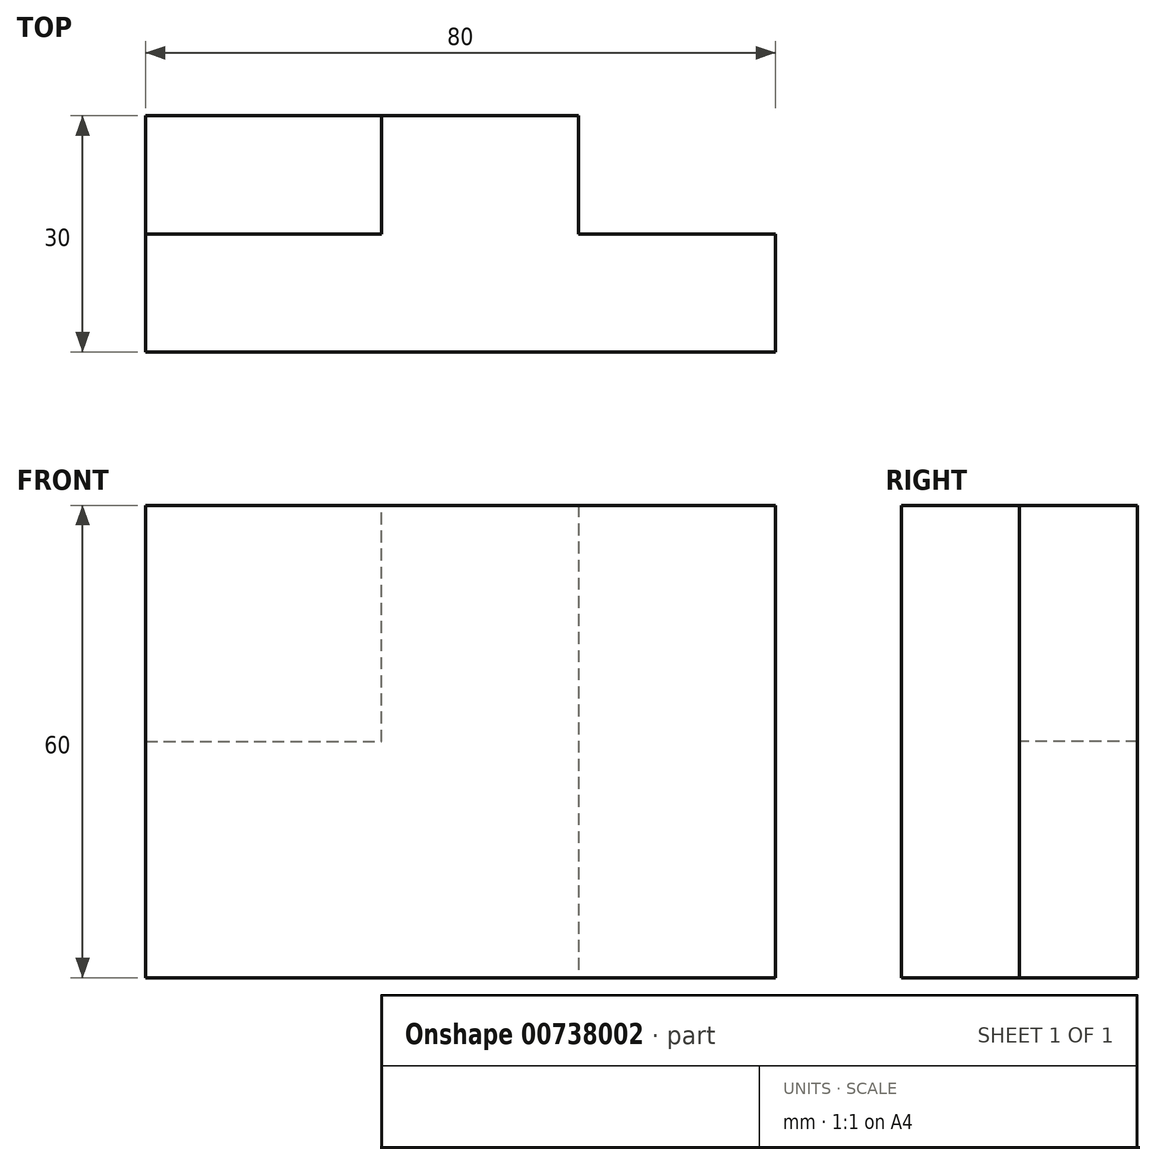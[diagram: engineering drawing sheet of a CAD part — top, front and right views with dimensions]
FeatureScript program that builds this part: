
annotation { "Feature Type Name" : "Feature", "Feature Type Description" : "" }
export const myFeature = defineFeature(function(context is Context, id is Id, definition is map)
    precondition{}
    {
        {
            var Q0;
            Q0=qCreatedBy(makeId("Front.planeOp"),FACE);
            var sketch = newSketch(context, id + "F0", { "sketchPlane" : qUnion([Q0])});
            skLineSegment(sketch, "E0", {"start": v(0, 0) * mm, "end": v(80, 0) * mm});
            skLineSegment(sketch, "E1", {"start": v(80, 0) * mm, "end": v(80, 60) * mm});
            skLineSegment(sketch, "E2", {"start": v(80, 60) * mm, "end": v(0, 60) * mm});
            skLineSegment(sketch, "E3", {"start": v(0, 60) * mm, "end": v(0, 0) * mm});
            skSolve(sketch);
        }
        {
            var Q0;
            Q0=makeQuery(id+"F0.imprint","IMPRINT",FACE,{"disambiguationData":[TD([[makeQuery(id+"F0.imprint","IMPRINT",EDGE,{"derivedFrom":sQuery(id+"F0.wireOp",EDGE,"E0")}),1.0]])]});
            extrude(context, id + "F1", {"entities" : qUnion([Q0]), "depth" : 15 * mm, "offsetDistance" : 25 * mm});
        }
        {
            var Q0;
            Q0=qCreatedBy(makeId("Front.planeOp"),FACE);
            var sketch = newSketch(context, id + "F2", { "sketchPlane" : qUnion([Q0])});
            skLineSegment(sketch, "E4", {"start": v(0, 0) * mm, "end": v(0, 30) * mm});
            skLineSegment(sketch, "E5", {"start": v(0, 30) * mm, "end": v(30, 30) * mm});
            skLineSegment(sketch, "E6", {"start": v(30, 30) * mm, "end": v(30, 60) * mm});
            skLineSegment(sketch, "E7", {"start": v(30, 60) * mm, "end": v(55, 60) * mm});
            skLineSegment(sketch, "E8", {"start": v(55, 60) * mm, "end": v(55, 0) * mm});
            skLineSegment(sketch, "E9", {"start": v(55, 0) * mm, "end": v(0, 0) * mm});
            skSolve(sketch);
        }
        {
            var Q0;
            Q0 = qSketchRegion(id + "F2", true);
            extrude(context, id + "F3", {"entities" : qUnion([Q0]), "operationType" : NewBodyOperationType.ADD, "oppositeDirection" : true, "depth" : 15 * mm, "offsetDistance" : 25 * mm});
        }
    });
